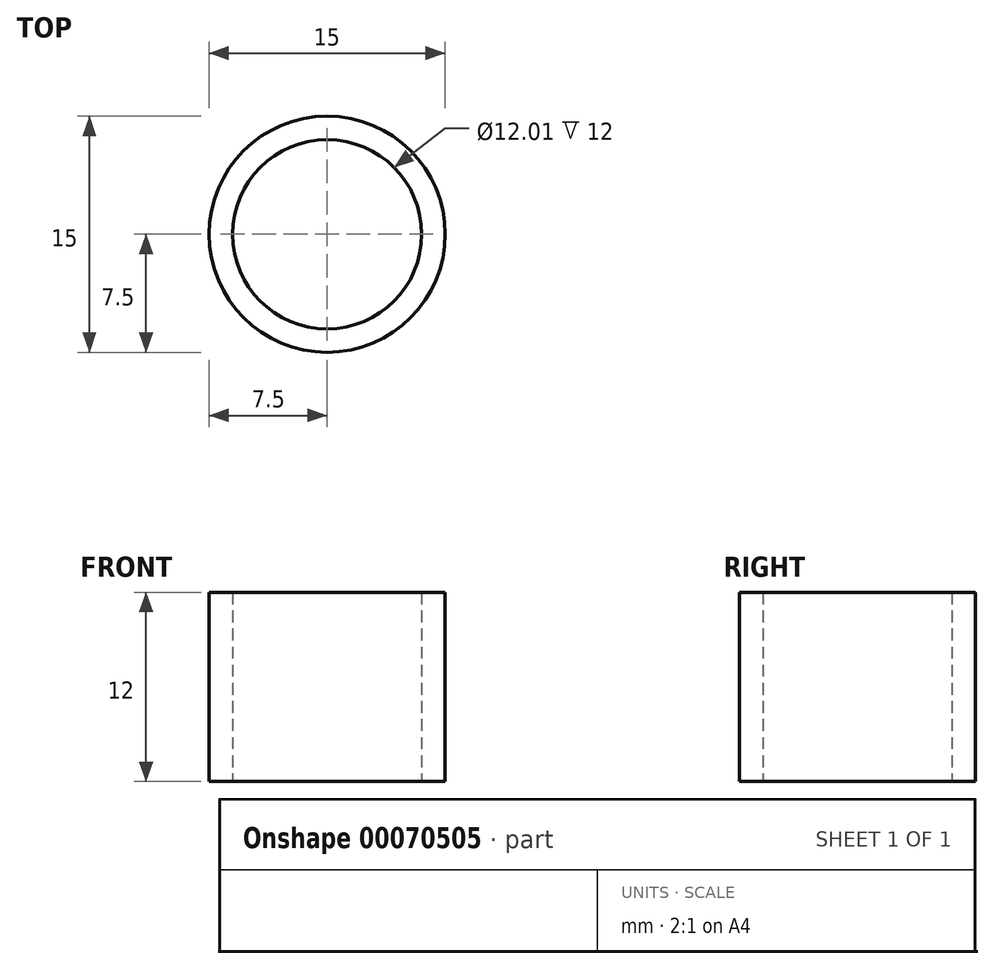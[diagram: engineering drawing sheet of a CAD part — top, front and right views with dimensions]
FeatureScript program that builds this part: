
annotation { "Feature Type Name" : "Feature", "Feature Type Description" : "" }
export const myFeature = defineFeature(function(context is Context, id is Id, definition is map)
    precondition{}
    {
        {
            var Q0;
            Q0=qCreatedBy(makeId("Top.planeOp"),FACE);
            var sketch = newSketch(context, id + "F0", { "sketchPlane" : qUnion([Q0])});
            skCircle(sketch, "E0", {"center": v(0, 0) * mm, "radius": 7.5 * mm});
            skCircle(sketch, "E1", {"center": v(0, 0) * mm, "radius": 6 * mm});
            skSolve(sketch);
        }
        {
            var Q0;
            Q0=makeQuery(id+"F0.imprint","IMPRINT",FACE,{"disambiguationData":[TD([[makeQuery(id+"F0.imprint","IMPRINT",EDGE,{"derivedFrom":sQuery(id+"F0.wireOp",EDGE,"E0")}),1.0]])]});
            extrude(context, id + "F1", {"entities" : qUnion([Q0]), "depth" : 12 * mm});
        }
    });
